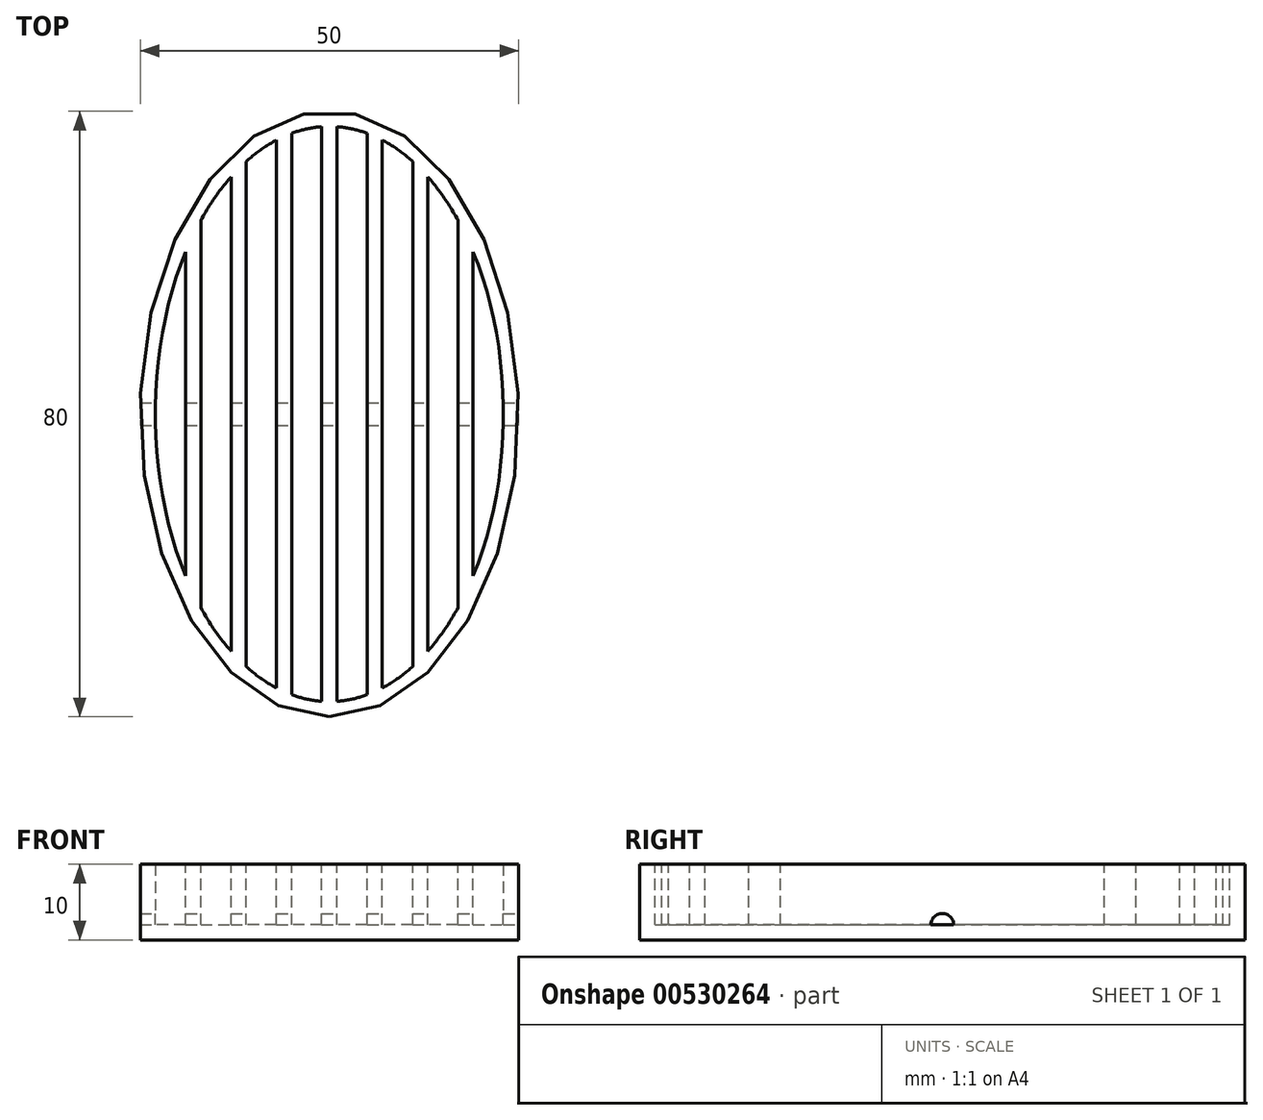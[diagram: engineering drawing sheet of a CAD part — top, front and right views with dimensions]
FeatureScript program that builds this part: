
annotation { "Feature Type Name" : "Feature", "Feature Type Description" : "" }
export const myFeature = defineFeature(function(context is Context, id is Id, definition is map)
    precondition{}
    {
        {
            var Q0;
            Q0=qCreatedBy(makeId("Top.planeOp"),FACE);
            var sketch = newSketch(context, id + "F0", { "sketchPlane" : qUnion([Q0])});
            skEllipse(sketch, "E0", {"center": v(0, 0) * mm, "majorRadius": 40 * mm, "minorRadius": 25 * mm, "majorAxis": v(0, -1)});
            skSolve(sketch);
        }
        {
            var Q0;
            Q0 = qSketchRegion(id + "F0", true);
            extrude(context, id + "F1", {"entities" : qUnion([Q0]), "depth" : 10 * mm, "offsetDistance" : 25 * mm});
        }
        {
            var Q0;
            Q0=makeQuery(id+"F1.opExtrude","CAP_FACE",FACE,{"disambiguationData":[OSD([sQuery(id+"F0.wireOp",EDGE,"E0")])],"isStart":false});
            var sketch = newSketch(context, id + "F2", { "sketchPlane" : qUnion([Q0])});
            skEllipticalArc(sketch, "E1", {});
            skLineSegment(sketch, "E2", {"start": v(-19, 21.41) * mm, "end": v(-19, -21.41) * mm});
            skPoint(sketch, "E3", {"position": v(-23, 0) * mm});
            skPoint(sketch, "E4", {"position": v(0, -38) * mm});
            skLineSegment(sketch, "E5", {"start": v(-17, 25.6) * mm, "end": v(-17, -25.6) * mm});
            skLineSegment(sketch, "E6", {"start": v(-13, 31.35) * mm, "end": v(-13, -31.35) * mm});
            skLineSegment(sketch, "E7", {"start": v(-11, -33.37) * mm, "end": v(-11, 33.37) * mm});
            skLineSegment(sketch, "E8", {"start": v(-7, 36.2) * mm, "end": v(-7, -36.2) * mm});
            skLineSegment(sketch, "E9", {"start": v(-5, -37.1) * mm, "end": v(-5, 37.1) * mm});
            skLineSegment(sketch, "E10", {"start": v(-1, 37.96) * mm, "end": v(-1, -38) * mm});
            skLineSegment(sketch, "E11", {"start": v(1, -37.96) * mm, "end": v(1, 37.96) * mm});
            skLineSegment(sketch, "E12", {"start": v(5, 37.1) * mm, "end": v(5, -37.1) * mm});
            skLineSegment(sketch, "E13", {"start": v(7, 36.2) * mm, "end": v(7, -36.2) * mm});
            skLineSegment(sketch, "E14", {"start": v(11, 33.37) * mm, "end": v(11, -33.37) * mm});
            skLineSegment(sketch, "E15", {"start": v(13, -31.35) * mm, "end": v(13, 31.35) * mm});
            skLineSegment(sketch, "E16", {"start": v(17, 25.6) * mm, "end": v(17, -25.6) * mm});
            skLineSegment(sketch, "E17", {"start": v(19, 21.41) * mm, "end": v(19, -21.41) * mm});
            skEllipticalArc(sketch, "E18.trimOffspring", {});
            skEllipticalArc(sketch, "E19.trimOffspring", {});
            skEllipticalArc(sketch, "E20.trimOffspring", {});
            skEllipticalArc(sketch, "E21.trimOffspring", {});
            skEllipticalArc(sketch, "E22.trimOffspring", {});
            skEllipticalArc(sketch, "E23.trimOffspring", {});
            skEllipticalArc(sketch, "E24.trimOffspring", {});
            skEllipticalArc(sketch, "E25.trimOffspring", {});
            skEllipticalArc(sketch, "E26.trimOffspring", {});
            skEllipticalArc(sketch, "E27.trimOffspring", {});
            skEllipticalArc(sketch, "E28.trimOffspring", {});
            skEllipticalArc(sketch, "E29.trimOffspring", {});
            skEllipticalArc(sketch, "E30.trimOffspring", {});
            const initialGuessF2  = {"E1": [0, 0, 0, -1, 0.038, 0.023, 4.1137209275491475, 5.311057033220233], "E18.trimOffspring": [0, 0, 0, -1, 0.038, 0.023, 5.451406859398608, 5.68248855424366], "E19.trimOffspring": [0, 0, 0, -1, 0.038, 0.023, 3.7422894065257175, 3.9733711013707707], "E20.trimOffspring": [0, 0, 0, -1, 0.038, 0.023, 3.450846354717306, 3.640266000651682], "E21.trimOffspring": [0, 0, 0, -1, 0.038, 0.023, 3.185084624379909, 3.3607337125873253], "E22.trimOffspring": [0, 0, 0, -1, 0.038, 0.023, 2.9224515945922604, 3.0981006827996787], "E23.trimOffspring": [0, 0, 0, -1, 0.038, 0.023, 2.6429193065279044, 2.8323389524622726], "E24.trimOffspring": [0, 0, 0, -1, 0.038, 0.023, 2.309814205808813, 2.5408959006538634], "E25.trimOffspring": [0, 0, 0, -1, 0.038, 0.023, 0.9721282739593543, 2.1694643796304387], "E26.trimOffspring": [0, 0, 0, -1, 0.038, 0.023, 0.6006967529359314, 0.8317784477809793], "E27.trimOffspring": [0, 0, 0, -1, 0.038, 0.023, 0.30925370112752043, 0.49867334706189037], "E28.trimOffspring": [0, 0, 0, -1, 0.038, 0.023, 0.04349197079011579, 0.2191410589975327], "E29.trimOffspring": [0, 0, 0, -1, 0.038, 0.023, 6.0640442481820545, 6.239693336389471], "E30.trimOffspring": [0, 0, 0, -1, 0.038, 0.023, 5.784511960117696, 5.973931606052073]};
            skSetInitialGuess(sketch, initialGuessF2);
            skSolve(sketch);
        }
        {
            var Q0;
            Q0=makeQuery(id+"F2.imprint","IMPRINT",FACE,{"disambiguationData":[TD([[makeQuery(id+"F2.imprint","IMPRINT",EDGE,{"derivedFrom":sQuery(id+"F2.wireOp",EDGE,"E1")}),1.0]])]});
            var Q1;
            Q1=makeQuery(id+"F2.imprint","IMPRINT",FACE,{"disambiguationData":[TD([[makeQuery(id+"F2.imprint","IMPRINT",EDGE,{"derivedFrom":sQuery(id+"F2.wireOp",EDGE,"E5")}),1.0]])]});
            var Q2;
            Q2=makeQuery(id+"F2.imprint","IMPRINT",FACE,{"disambiguationData":[TD([[makeQuery(id+"F2.imprint","IMPRINT",EDGE,{"derivedFrom":sQuery(id+"F2.wireOp",EDGE,"E7")}),-1.0]])]});
            var Q3;
            Q3=makeQuery(id+"F2.imprint","IMPRINT",FACE,{"disambiguationData":[TD([[makeQuery(id+"F2.imprint","IMPRINT",EDGE,{"derivedFrom":sQuery(id+"F2.wireOp",EDGE,"E9")}),-1.0]])]});
            var Q4;
            Q4=makeQuery(id+"F2.imprint","IMPRINT",FACE,{"disambiguationData":[TD([[makeQuery(id+"F2.imprint","IMPRINT",EDGE,{"derivedFrom":sQuery(id+"F2.wireOp",EDGE,"E11")}),-1.0]])]});
            var Q5;
            Q5=makeQuery(id+"F2.imprint","IMPRINT",FACE,{"disambiguationData":[TD([[makeQuery(id+"F2.imprint","IMPRINT",EDGE,{"derivedFrom":sQuery(id+"F2.wireOp",EDGE,"E13")}),1.0]])]});
            var Q6;
            Q6=makeQuery(id+"F2.imprint","IMPRINT",FACE,{"disambiguationData":[TD([[makeQuery(id+"F2.imprint","IMPRINT",EDGE,{"derivedFrom":sQuery(id+"F2.wireOp",EDGE,"E15")}),-1.0]])]});
            var Q7;
            Q7=makeQuery(id+"F2.imprint","IMPRINT",FACE,{"disambiguationData":[TD([[makeQuery(id+"F2.imprint","IMPRINT",EDGE,{"derivedFrom":sQuery(id+"F2.wireOp",EDGE,"E17")}),1.0]])]});
            extrude(context, id + "F3", {"entities" : qUnion([Q0, Q1, Q2, Q3, Q4, Q5, Q6, Q7]), "operationType" : NewBodyOperationType.REMOVE, "oppositeDirection" : true, "depth" : 8 * mm, "offsetDistance" : 25 * mm});
        }
        {
            var Q0;
            Q0=qCreatedBy(makeId("Right.planeOp"),FACE);
            var sketch = newSketch(context, id + "F4", { "sketchPlane" : qUnion([Q0])});
            skLineSegment(sketch, "E31", {"start": v(-1.5, 2) * mm, "end": v(1.5, 2) * mm});
            skArc(sketch, "E32", {"start": v(1.5, 2) * mm, "mid": v(0, 3.5) * mm, "end": v(-1.5, 2) * mm});
            skSolve(sketch);
        }
        {
            var Q0;
            Q0 = qSketchRegion(id + "F4", true);
            extrude(context, id + "F5", {"entities" : qUnion([Q0]), "operationType" : NewBodyOperationType.REMOVE, "endBound" : BoundingType.SYMMETRIC, "oppositeDirection" : true, "depth" : 100 * mm, "offsetDistance" : 25 * mm});
        }
    });
